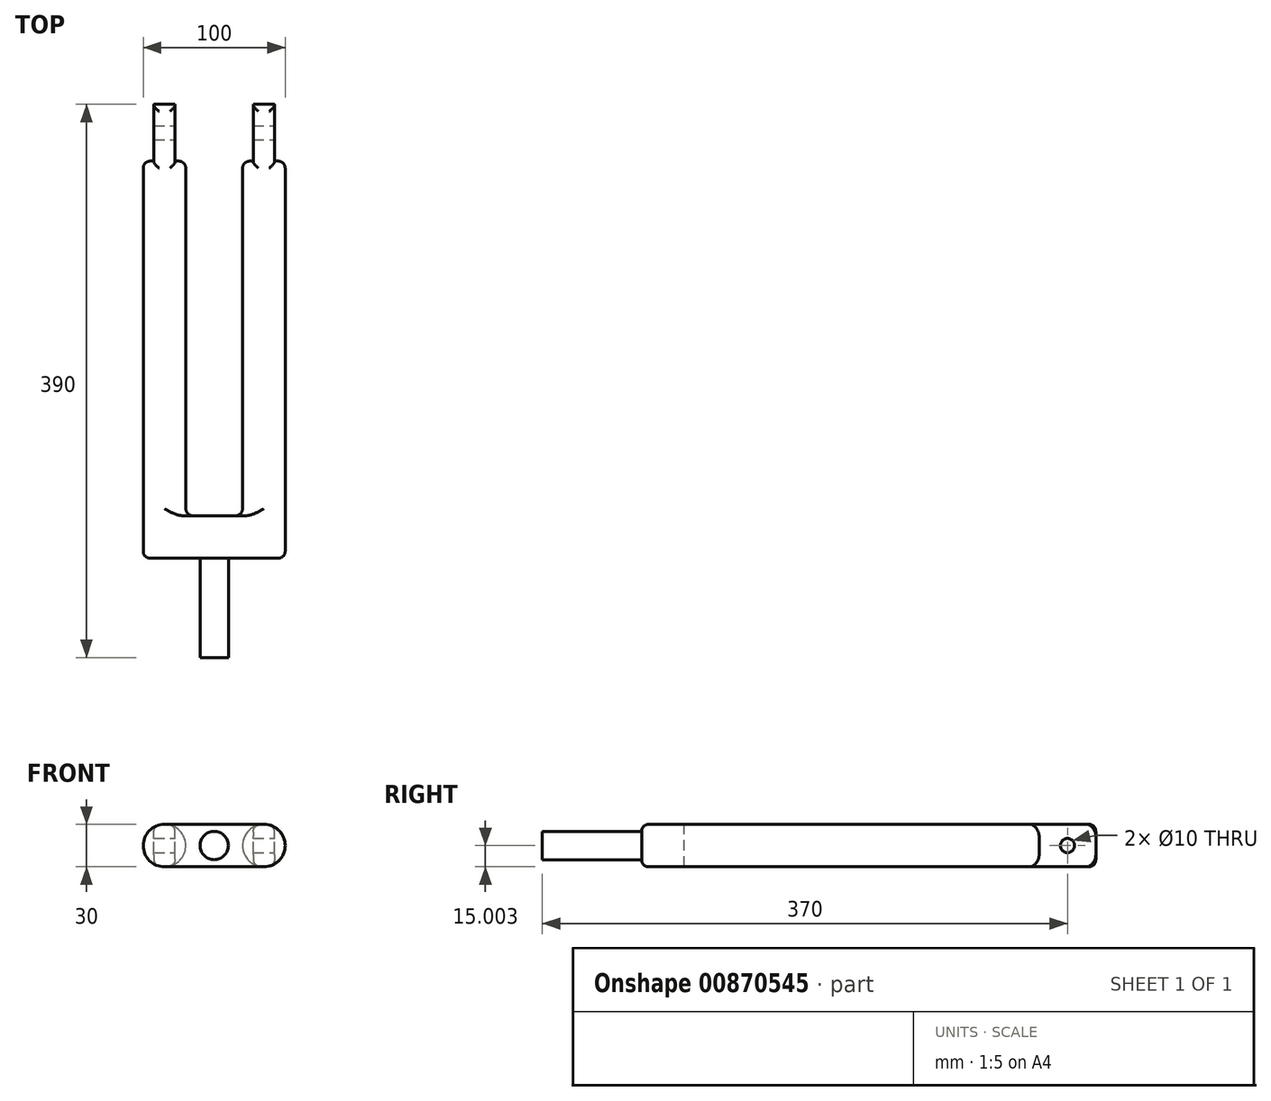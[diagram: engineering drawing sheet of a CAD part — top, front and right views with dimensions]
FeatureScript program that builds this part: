
annotation { "Feature Type Name" : "Feature", "Feature Type Description" : "" }
export const myFeature = defineFeature(function(context is Context, id is Id, definition is map)
    precondition{}
    {
        {
            var Q0;
            Q0=qCreatedBy(makeId("Front.planeOp"),FACE);
            var sketch = newSketch(context, id + "F0", { "sketchPlane" : qUnion([Q0])});
            skLineSegment(sketch, "E0.bottom", {"start": v(-55, 27.15) * mm, "end": v(15, 27.15) * mm});
            skLineSegment(sketch, "E0.top", {"start": v(-55, 57.15) * mm, "end": v(15, 57.15) * mm});
            skPoint(sketch, "E1", {"position": v(-20, 42.15) * mm});
            skCircle(sketch, "E2", {"center": v(-20, 42.15) * mm, "radius": 10 * mm});
            skLineSegment(sketch, "E3", {"start": v(-40, 57.15) * mm, "end": v(-40, 27.15) * mm});
            skLineSegment(sketch, "E4", {"start": v(0, 27.15) * mm, "end": v(0, 57.15) * mm});
            skCircle(sketch, "E5", {"center": v(-55, 42.15) * mm, "radius": 15 * mm});
            skCircle(sketch, "E6", {"center": v(15, 42.15) * mm, "radius": 15 * mm});
            skPoint(sketch, "E6.centerSnap0", {"position": v(0, 42.15) * mm});
            skPoint(sketch, "E7.orphan", {"position": v(-70, 27.15) * mm});
            skPoint(sketch, "E8.orphan", {"position": v(30, 57.15) * mm});
            skSolve(sketch);
        }
        {
            var Q0;
            {var subQ0=sQuery(id+"F0.wireOp",EDGE,"E5");var subQ1=makeQuery(id+"F0.imprint","INTERSECT",VERTEX,{"derivedFrom":[sQuery(id+"F0.wireOp",EDGE,"E0.top"),subQ0]});Q0=makeQuery(id+"F0.imprint","IMPRINT",FACE,{"disambiguationData":[TD([[makeQuery(id+"F0.imprint","IMPRINT",EDGE,{"disambiguationData":[TD([[subQ1,1.0]])],"derivedFrom":subQ0}),1.0]])]});}
            var Q1;
            Q1=makeQuery(id+"F0.imprint","IMPRINT",FACE,{"disambiguationData":[TD([[makeQuery(id+"F0.imprint","IMPRINT",EDGE,{"derivedFrom":sQuery(id+"F0.wireOp",EDGE,"E2")}),-1.0]])]});
            var Q2;
            {var subQ0=sQuery(id+"F0.wireOp",EDGE,"E5");var subQ1=sQuery(id+"F0.wireOp",EDGE,"E0.top");var subQ2=makeQuery(id+"F0.imprint","INTERSECT",VERTEX,{"derivedFrom":[subQ1,subQ0]});Q2=makeQuery(id+"F0.imprint","IMPRINT",FACE,{"disambiguationData":[TD([[makeQuery(id+"F0.imprint","IMPRINT",EDGE,{"disambiguationData":[TD([[subQ2,-1.0]])],"derivedFrom":subQ1}),-1.0]])]});}
            var Q3;
            {var subQ0=sQuery(id+"F0.wireOp",EDGE,"E5");var subQ1=sQuery(id+"F0.wireOp",EDGE,"E0.bottom");var subQ2=makeQuery(id+"F0.imprint","INTERSECT",VERTEX,{"derivedFrom":[subQ1,subQ0]});Q3=makeQuery(id+"F0.imprint","IMPRINT",FACE,{"disambiguationData":[TD([[makeQuery(id+"F0.imprint","IMPRINT",EDGE,{"disambiguationData":[TD([[subQ2,-1.0]])],"derivedFrom":subQ1}),1.0]])]});}
            var Q4;
            {var subQ0=sQuery(id+"F0.wireOp",EDGE,"E6");var subQ1=sQuery(id+"F0.wireOp",EDGE,"E0.bottom");var subQ2=makeQuery(id+"F0.imprint","INTERSECT",VERTEX,{"derivedFrom":[subQ1,subQ0]});Q4=makeQuery(id+"F0.imprint","IMPRINT",FACE,{"disambiguationData":[TD([[makeQuery(id+"F0.imprint","IMPRINT",EDGE,{"disambiguationData":[TD([[subQ2,1.0]])],"derivedFrom":subQ1}),1.0]])]});}
            var Q5;
            {var subQ0=sQuery(id+"F0.wireOp",EDGE,"E6");var subQ1=makeQuery(id+"F0.imprint","INTERSECT",VERTEX,{"derivedFrom":[sQuery(id+"F0.wireOp",EDGE,"E0.top"),subQ0]});Q5=makeQuery(id+"F0.imprint","IMPRINT",FACE,{"disambiguationData":[TD([[makeQuery(id+"F0.imprint","IMPRINT",EDGE,{"disambiguationData":[TD([[subQ1,-1.0]])],"derivedFrom":subQ0}),1.0]])]});}
            var Q6;
            {var subQ0=sQuery(id+"F0.wireOp",EDGE,"E6");var subQ1=sQuery(id+"F0.wireOp",EDGE,"E0.top");var subQ2=makeQuery(id+"F0.imprint","INTERSECT",VERTEX,{"derivedFrom":[subQ1,subQ0]});Q6=makeQuery(id+"F0.imprint","IMPRINT",FACE,{"disambiguationData":[TD([[makeQuery(id+"F0.imprint","IMPRINT",EDGE,{"disambiguationData":[TD([[subQ2,1.0]])],"derivedFrom":subQ1}),-1.0]])]});}
            extrude(context, id + "F1", {"entities" : qUnion([Q0, Q1, Q2, Q3, Q4, Q5, Q6]), "depth" : 30 * mm, "offsetDistance" : 25 * mm});
        }
        {
            var Q0;
            {var subQ0=sQuery(id+"F0.wireOp",EDGE,"E5");var subQ1=makeQuery(id+"F0.imprint","INTERSECT",VERTEX,{"derivedFrom":[sQuery(id+"F0.wireOp",EDGE,"E0.top"),subQ0]});Q0=makeQuery(id+"F0.imprint","IMPRINT",FACE,{"disambiguationData":[TD([[makeQuery(id+"F0.imprint","IMPRINT",EDGE,{"disambiguationData":[TD([[subQ1,1.0]])],"derivedFrom":subQ0}),1.0]])]});}
            var Q1;
            {var subQ0=sQuery(id+"F0.wireOp",EDGE,"E6");var subQ1=makeQuery(id+"F0.imprint","INTERSECT",VERTEX,{"derivedFrom":[sQuery(id+"F0.wireOp",EDGE,"E0.top"),subQ0]});Q1=makeQuery(id+"F0.imprint","IMPRINT",FACE,{"disambiguationData":[TD([[makeQuery(id+"F0.imprint","IMPRINT",EDGE,{"disambiguationData":[TD([[subQ1,-1.0]])],"derivedFrom":subQ0}),1.0]])]});}
            extrude(context, id + "F2", {"entities" : qUnion([Q0, Q1]), "operationType" : NewBodyOperationType.ADD, "depth" : -250 * mm, "offsetDistance" : 25 * mm});
        }
        {
            var Q0;
            Q0=makeQuery(id+"F2.opExtrude","CAP_FACE",FACE,{"disambiguationData":[OSD([sQuery(id+"F0.wireOp",EDGE,"E6")])],"isStart":false});
            var sketch = newSketch(context, id + "F3", { "sketchPlane" : qUnion([Q0])});
            skLineSegment(sketch, "E9.bottom", {"start": v(-7.5, 27.15) * mm, "end": v(-15, 27.15) * mm});
            skLineSegment(sketch, "E9.top", {"start": v(-7.5, 57.15) * mm, "end": v(-15, 57.15) * mm});
            skLineSegment(sketch, "E9.right", {"start": v(-22.5, 29.16) * mm, "end": v(-22.5, 55.14) * mm});
            skArc(sketch, "E10", {"start": v(-22.5, 29.16) * mm, "mid": v(-18.88, 27.66) * mm, "end": v(-15, 27.15) * mm});
            skLineSegment(sketch, "E11", {"start": v(-7.5, 27.15) * mm, "end": v(-7.5, 57.15) * mm});
            skArc(sketch, "E12.trimOffspring", {"start": v(-15, 57.15) * mm, "mid": v(-18.88, 56.64) * mm, "end": v(-22.5, 55.14) * mm});
            skArc(sketch, "E13", {"start": v(62.5, 55.14) * mm, "mid": v(55, 57.15) * mm, "end": v(47.5, 55.14) * mm});
            skLineSegment(sketch, "E14.left", {"start": v(47.5, 29.16) * mm, "end": v(47.5, 55.14) * mm});
            skLineSegment(sketch, "E14.right", {"start": v(62.5, 29.16) * mm, "end": v(62.5, 55.14) * mm});
            skPoint(sketch, "E15.orphan", {"position": v(62.5, 57.15) * mm});
            skPoint(sketch, "E16.orphan", {"position": v(47.5, 57.15) * mm});
            skArc(sketch, "E17.trimOffspring", {"start": v(47.5, 29.16) * mm, "mid": v(55, 27.15) * mm, "end": v(62.5, 29.16) * mm});
            skSolve(sketch);
        }
        {
            var Q0;
            Q0=makeQuery(id+"F3.imprint","IMPRINT",FACE,{"disambiguationData":[TD([[makeQuery(id+"F3.imprint","IMPRINT",EDGE,{"derivedFrom":sQuery(id+"F3.wireOp",EDGE,"E9.right")}),-1.0]])]});
            var Q1;
            Q1=makeQuery(id+"F3.imprint","IMPRINT",FACE,{"disambiguationData":[TD([[makeQuery(id+"F3.imprint","IMPRINT",EDGE,{"derivedFrom":sQuery(id+"F3.wireOp",EDGE,"E13")}),1.0]])]});
            extrude(context, id + "F4", {"entities" : qUnion([Q0, Q1]), "operationType" : NewBodyOperationType.ADD, "depth" : 40 * mm, "offsetDistance" : 25 * mm});
        }
        {
            var Q0;
            Q0=makeQuery(id+"F4.opExtrude","SWEPT_FACE",FACE,{"disambiguationData":[OSD([sQuery(id+"F3.wireOp",EDGE,"E9.right")])]});
            var sketch = newSketch(context, id + "F5", { "sketchPlane" : qUnion([Q0])});
            skPoint(sketch, "E18", {"position": v(270, 42.15) * mm});
            skSolve(sketch);
        }
        {
            var Q0;
            Q0=sQuery(id+"F5.wireOp",VERTEX,"E18");
            var Q1;
            Q1=makeQuery(id+"F1.opExtrude","SWEPT_BODY",BODY,{"disambiguationData":[OSD([sQuery(id+"F0.wireOp",EDGE,"E0.bottom"),sQuery(id+"F0.wireOp",EDGE,"E0.top"),sQuery(id+"F0.wireOp",EDGE,"E2"),sQuery(id+"F0.wireOp",EDGE,"E5"),sQuery(id+"F0.wireOp",EDGE,"E6")])]});
            hole(context, id + "F6", {"style" : HoleStyle.SIMPLE, "endStyle" : HoleEndStyle.THROUGH, "holeDiameter" : 10 * mm, "majorDiameter" : 5 * mm, "isTappedThrough" : true, "tappedDepth" : 12 * mm, "tapClearance" : 3, "locations" : qUnion([Q0]), "scope" : qUnion([Q1])});
        }
        {
            var Q0;
            Q0=makeQuery(id+"F0.imprint","IMPRINT",FACE,{"disambiguationData":[TD([[makeQuery(id+"F0.imprint","IMPRINT",EDGE,{"derivedFrom":sQuery(id+"F0.wireOp",EDGE,"E2")}),1.0]])]});
            extrude(context, id + "F7", {"entities" : qUnion([Q0]), "operationType" : NewBodyOperationType.ADD, "depth" : 100 * mm, "offsetDistance" : 25 * mm});
        }
        {
            var Q0;
            {var subQ0=sQuery(id+"F0.wireOp",EDGE,"E6");Q0=makeQuery(id+"F4.boolean.opBoolean","MERGE",FACE,{"derivedFrom":[makeQuery(id+"F2.boolean.opBoolean","MERGE",FACE,{"derivedFrom":[makeQuery(id+"F1.opExtrude","SWEPT_FACE",FACE,{"disambiguationData":[OSD([subQ0])]}),makeQuery(id+"F2.opExtrude","SWEPT_FACE",FACE,{"disambiguationData":[OSD([subQ0])]})]}),makeQuery(id+"F4.opExtrude","SWEPT_FACE",FACE,{"disambiguationData":[OSD([subQ0,sQuery(id+"F3.wireOp",EDGE,"E10")])]}),makeQuery(id+"F4.opExtrude","SWEPT_FACE",FACE,{"disambiguationData":[OSD([subQ0,sQuery(id+"F3.wireOp",EDGE,"E12.trimOffspring")])]})]});}
            fillet(context, id + "F8", {"entities" : qUnion([Q0]), "radius" : 5 * mm, "tangentPropagation" : true, "allowEdgeOverflow" : false});
        }
        {
            var Q0;
            {var subQ0=sQuery(id+"F0.wireOp",EDGE,"E5");Q0=makeQuery(id+"F4.boolean.opBoolean","MERGE",FACE,{"derivedFrom":[makeQuery(id+"F2.boolean.opBoolean","MERGE",FACE,{"derivedFrom":[makeQuery(id+"F1.opExtrude","SWEPT_FACE",FACE,{"disambiguationData":[OSD([subQ0])]}),makeQuery(id+"F2.opExtrude","SWEPT_FACE",FACE,{"disambiguationData":[OSD([subQ0])]})]}),makeQuery(id+"F4.opExtrude","SWEPT_FACE",FACE,{"disambiguationData":[OSD([sQuery(id+"F3.wireOp",EDGE,"E13")])]}),makeQuery(id+"F4.opExtrude","SWEPT_FACE",FACE,{"disambiguationData":[OSD([sQuery(id+"F3.wireOp",EDGE,"E17.trimOffspring")])]})]});}
            fillet(context, id + "F9", {"entities" : qUnion([Q0]), "radius" : 5 * mm, "tangentPropagation" : true, "allowEdgeOverflow" : false});
        }
    });
